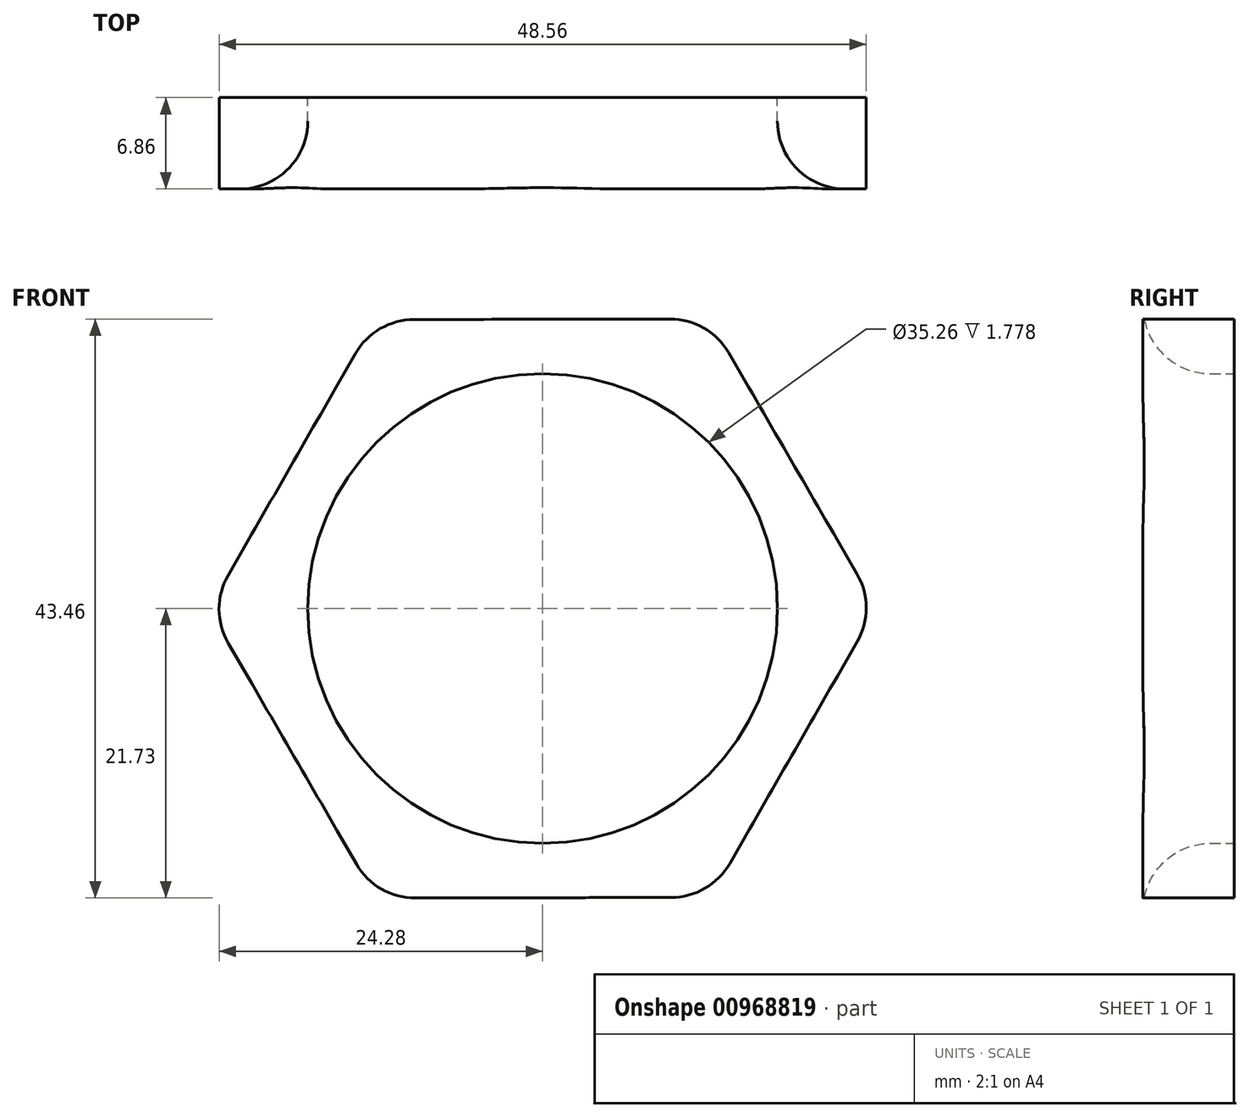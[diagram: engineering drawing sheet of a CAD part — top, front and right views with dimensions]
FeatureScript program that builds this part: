
annotation { "Feature Type Name" : "Feature", "Feature Type Description" : "" }
export const myFeature = defineFeature(function(context is Context, id is Id, definition is map)
    precondition{}
    {
        {
            var Q0;
            Q0=qCreatedBy(makeId("Front.planeOp"),FACE);
            var sketch = newSketch(context, id + "F0", { "sketchPlane" : qUnion([Q0])});
            skCircle(sketch, "E0", {"center": v(0, 0) * mm, "radius": 1 * mm});
            skCircle(sketch, "E1", {"center": v(0, 0) * mm, "radius": 17.63 * mm});
            skCircle(sketch, "E2.cCircle", {"center": v(0, 0) * mm, "radius": 21.7 * mm, "construction": true});
            skLineSegment(sketch, "E2.0", {"start": v(12.49, 21.74) * mm, "end": v(25.07, 0.05) * mm});
            skLineSegment(sketch, "E2.1", {"start": v(25.07, 0.05) * mm, "end": v(12.58, -21.68) * mm});
            skLineSegment(sketch, "E2.2", {"start": v(12.58, -21.68) * mm, "end": v(-12.49, -21.74) * mm});
            skLineSegment(sketch, "E2.3", {"start": v(-12.49, -21.74) * mm, "end": v(-25.07, -0.05) * mm});
            skLineSegment(sketch, "E2.4", {"start": v(-25.07, -0.05) * mm, "end": v(-12.58, 21.68) * mm});
            skLineSegment(sketch, "E2.5", {"start": v(-12.58, 21.68) * mm, "end": v(12.49, 21.74) * mm});
            skPoint(sketch, "E2.0.midPoint", {"position": v(18.78, 10.9) * mm});
            skSolve(sketch);
        }
        {
            var Q0;
            Q0 = qSketchRegion(id + "F0", true);
            extrude(context, id + "F1", {"entities" : qUnion([Q0]), "depth" : 6.86 * mm, "offsetDistance" : 25.4 * mm});
        }
        {
            var Q0;
            Q0=makeQuery(id+"F1.opExtrude","CAP_EDGE",EDGE,{"disambiguationData":[OSD([sQuery(id+"F0.wireOp",EDGE,"E1")])],"isStart":false});
            var Q1;
            Q1=makeQuery(id+"F1.opExtrude","SWEPT_EDGE",EDGE,{"disambiguationData":[OSD([sQuery(id+"F0.wireOp",EDGE,"E2.3"),sQuery(id+"F0.wireOp",EDGE,"E2.4")])]});
            var Q2;
            Q2=makeQuery(id+"F1.opExtrude","SWEPT_EDGE",EDGE,{"disambiguationData":[OSD([sQuery(id+"F0.wireOp",EDGE,"E2.2"),sQuery(id+"F0.wireOp",EDGE,"E2.3")])]});
            var Q3;
            Q3=makeQuery(id+"F1.opExtrude","SWEPT_EDGE",EDGE,{"disambiguationData":[OSD([sQuery(id+"F0.wireOp",EDGE,"E2.1"),sQuery(id+"F0.wireOp",EDGE,"E2.2")])]});
            var Q4;
            Q4=makeQuery(id+"F1.opExtrude","SWEPT_EDGE",EDGE,{"disambiguationData":[OSD([sQuery(id+"F0.wireOp",EDGE,"E2.0"),sQuery(id+"F0.wireOp",EDGE,"E2.1")])]});
            var Q5;
            Q5=makeQuery(id+"F1.opExtrude","SWEPT_EDGE",EDGE,{"disambiguationData":[OSD([sQuery(id+"F0.wireOp",EDGE,"E2.0"),sQuery(id+"F0.wireOp",EDGE,"E2.5")])]});
            var Q6;
            Q6=makeQuery(id+"F1.opExtrude","SWEPT_EDGE",EDGE,{"disambiguationData":[OSD([sQuery(id+"F0.wireOp",EDGE,"E2.4"),sQuery(id+"F0.wireOp",EDGE,"E2.5")])]});
            fillet(context, id + "F2", {"entities" : qUnion([Q0, Q1, Q2, Q3, Q4, Q5, Q6]), "radius" : 5.08 * mm, "tangentPropagation" : true, "allowEdgeOverflow" : false});
        }
    });
